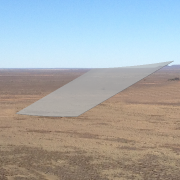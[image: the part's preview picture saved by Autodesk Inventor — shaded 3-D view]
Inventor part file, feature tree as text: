
AUTODESK INVENTOR PART (.ipt)
format: ipt  version: 2013 SP2 (Build 170200200, 200)  size: 150,528 bytes
history: native  units: in
note: dims shown in document units (in); Inventor stores cm internally (conversion verified against a paired STEP export)
features: sketch x3, sweep x1, extrude x1, other x1
ambient origin geometry x8: Origin, YZ Plane, XZ Plane, XY Plane, X Axis, Y Axis, Z Axis, Center Point
feature tree (6):
  sweep  "Sweep2"
  extrude  "Extrusion3"  TaperAngle=0.0deg  [1 undecoded]
  sketch  "Sketch3"  dims[d6=0.0in d7=277.0in d8=90.0in]
  other  "2D Equation Curve2"
  sketch  "Sketch4"  dims[d10=0.25in d11=0.0in]
  sketch  "Sketch8"  dims[d28=2.0in d29=2.0in d32=2.0in d33=300.0in d34=1.1853in d35=163.0in d36=206.0in d37=300.0in d38=0.0in]
note: 1 required parameter value undecoded (feature->parameter linkage not recoverable at this tier; creation-order binding heuristic only, values carry confidence <= 0.55)
